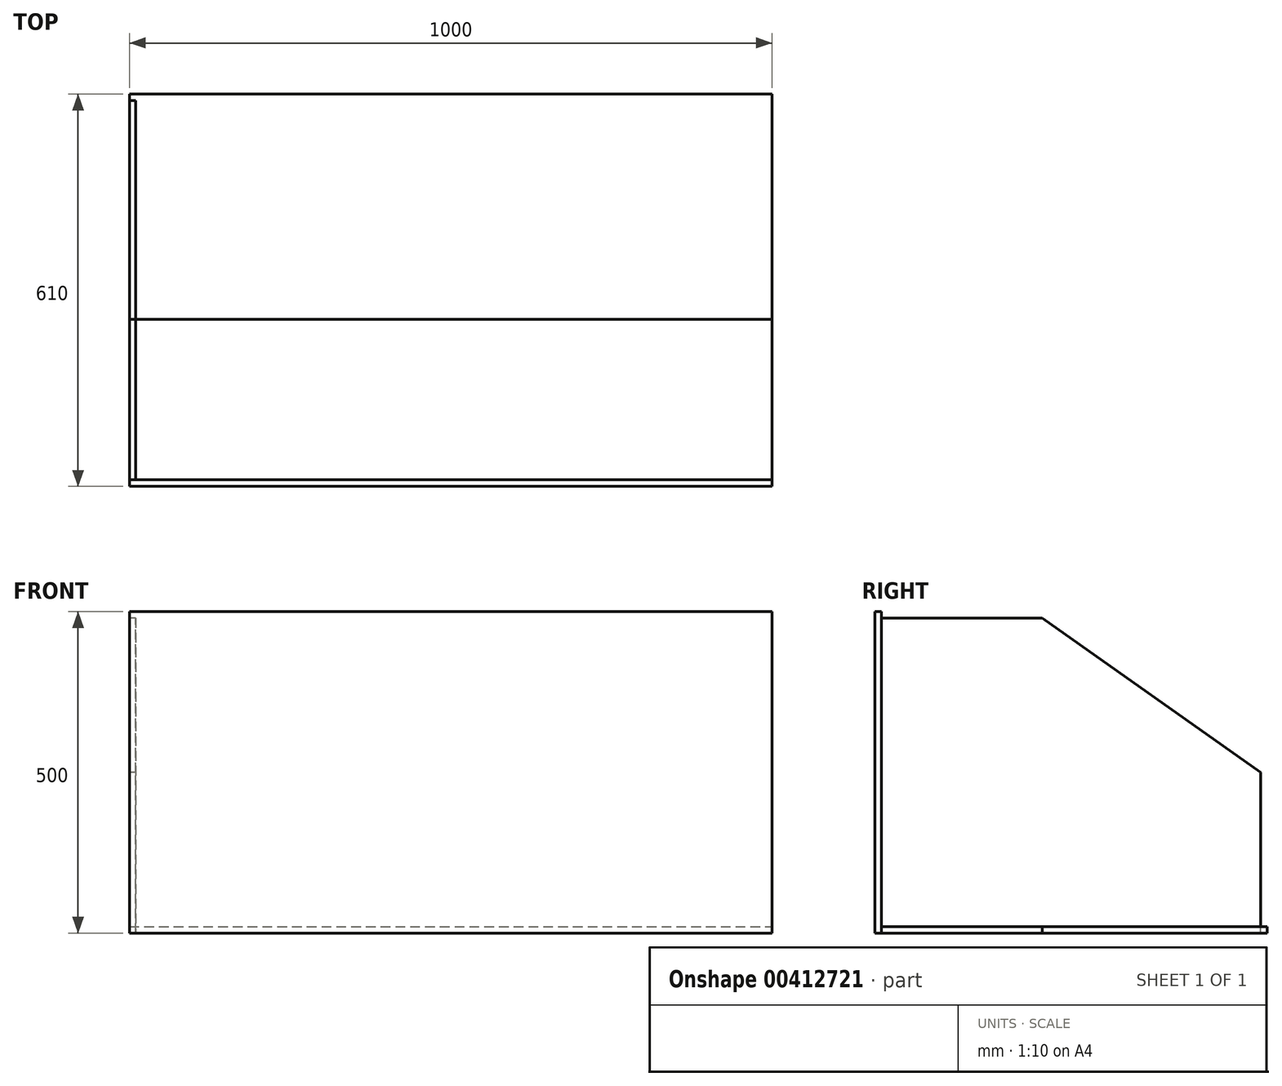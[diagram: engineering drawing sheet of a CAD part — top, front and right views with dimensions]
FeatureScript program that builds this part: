
annotation { "Feature Type Name" : "Feature", "Feature Type Description" : "" }
export const myFeature = defineFeature(function(context is Context, id is Id, definition is map)
    precondition{}
    {
        {
            var Q0;
            Q0=qCreatedBy(makeId("Top.planeOp"),FACE);
            var sketch = newSketch(context, id + "F0", { "sketchPlane" : qUnion([Q0])});
            skLineSegment(sketch, "E0.bottom", {"start": v(0, 0) * mm, "end": v(1000, 0) * mm});
            skLineSegment(sketch, "E0.top", {"start": v(0, 600) * mm, "end": v(1000, 600) * mm});
            skLineSegment(sketch, "E0.left", {"start": v(0, 0) * mm, "end": v(0, 600) * mm});
            skLineSegment(sketch, "E0.right", {"start": v(1000, 0) * mm, "end": v(1000, 600) * mm});
            skSolve(sketch);
        }
        {
            var Q0;
            Q0=makeQuery(id+"F0.imprint","IMPRINT",FACE,{"disambiguationData":[TD([[makeQuery(id+"F0.imprint","IMPRINT",EDGE,{"derivedFrom":sQuery(id+"F0.wireOp",EDGE,"E0.bottom")}),1.0]])]});
            extrude(context, id + "F1", {"entities" : qUnion([Q0]), "depth" : 10 * mm});
        }
        {
            var Q0;
            Q0=qCreatedBy(makeId("Front.planeOp"),FACE);
            var sketch = newSketch(context, id + "F2", { "sketchPlane" : qUnion([Q0])});
            skLineSegment(sketch, "E1.bottom", {"start": v(0, 0) * mm, "end": v(1000, 0) * mm});
            skLineSegment(sketch, "E1.top", {"start": v(0, 500) * mm, "end": v(1000, 500) * mm});
            skLineSegment(sketch, "E1.left", {"start": v(0, 0) * mm, "end": v(0, 500) * mm});
            skLineSegment(sketch, "E1.right", {"start": v(1000, 0) * mm, "end": v(1000, 500) * mm});
            skSolve(sketch);
        }
        {
            var Q0;
            Q0=makeQuery(id+"F2.imprint","IMPRINT",FACE,{"disambiguationData":[TD([[makeQuery(id+"F2.imprint","IMPRINT",EDGE,{"derivedFrom":sQuery(id+"F2.wireOp",EDGE,"E1.bottom")}),1.0]])]});
            extrude(context, id + "F3", {"entities" : qUnion([Q0]), "depth" : 10 * mm});
        }
        {
            var Q0;
            Q0=qCreatedBy(makeId("Right.planeOp"),FACE);
            var sketch = newSketch(context, id + "F4", { "sketchPlane" : qUnion([Q0])});
            skLineSegment(sketch, "E2", {"start": v(0, 0) * mm, "end": v(590, 0) * mm});
            skLineSegment(sketch, "E3", {"start": v(590, 0) * mm, "end": v(590, 250) * mm});
            skLineSegment(sketch, "E4", {"start": v(590, 250) * mm, "end": v(250, 490) * mm});
            skLineSegment(sketch, "E5", {"start": v(250, 490) * mm, "end": v(0, 490) * mm});
            skLineSegment(sketch, "E6", {"start": v(0, 490) * mm, "end": v(0, 0) * mm});
            skSolve(sketch);
        }
        {
            var Q0;
            Q0=makeQuery(id+"F4.imprint","IMPRINT",FACE,{"disambiguationData":[TD([[makeQuery(id+"F4.imprint","IMPRINT",EDGE,{"derivedFrom":sQuery(id+"F4.wireOp",EDGE,"E2")}),1.0]])]});
            extrude(context, id + "F5", {"entities" : qUnion([Q0]), "depth" : 10 * mm});
        }
        {
            var Q0;
            Q0=qCreatedBy(makeId("Top.planeOp"),FACE);
            var sketch = newSketch(context, id + "F6", { "sketchPlane" : qUnion([Q0])});
            skLineSegment(sketch, "E7.bottom", {"start": v(0, 0) * mm, "end": v(1000, 0) * mm});
            skLineSegment(sketch, "E7.top", {"start": v(0, 250) * mm, "end": v(1000, 250) * mm});
            skLineSegment(sketch, "E7.left", {"start": v(0, 0) * mm, "end": v(0, 250) * mm});
            skLineSegment(sketch, "E7.right", {"start": v(1000, 0) * mm, "end": v(1000, 250) * mm});
            skSolve(sketch);
        }
        {
            var Q0;
            Q0 = qSketchRegion(id + "F6", true);
            extrude(context, id + "F7", {"entities" : qUnion([Q0]), "depth" : 10 * mm});
        }
    });
